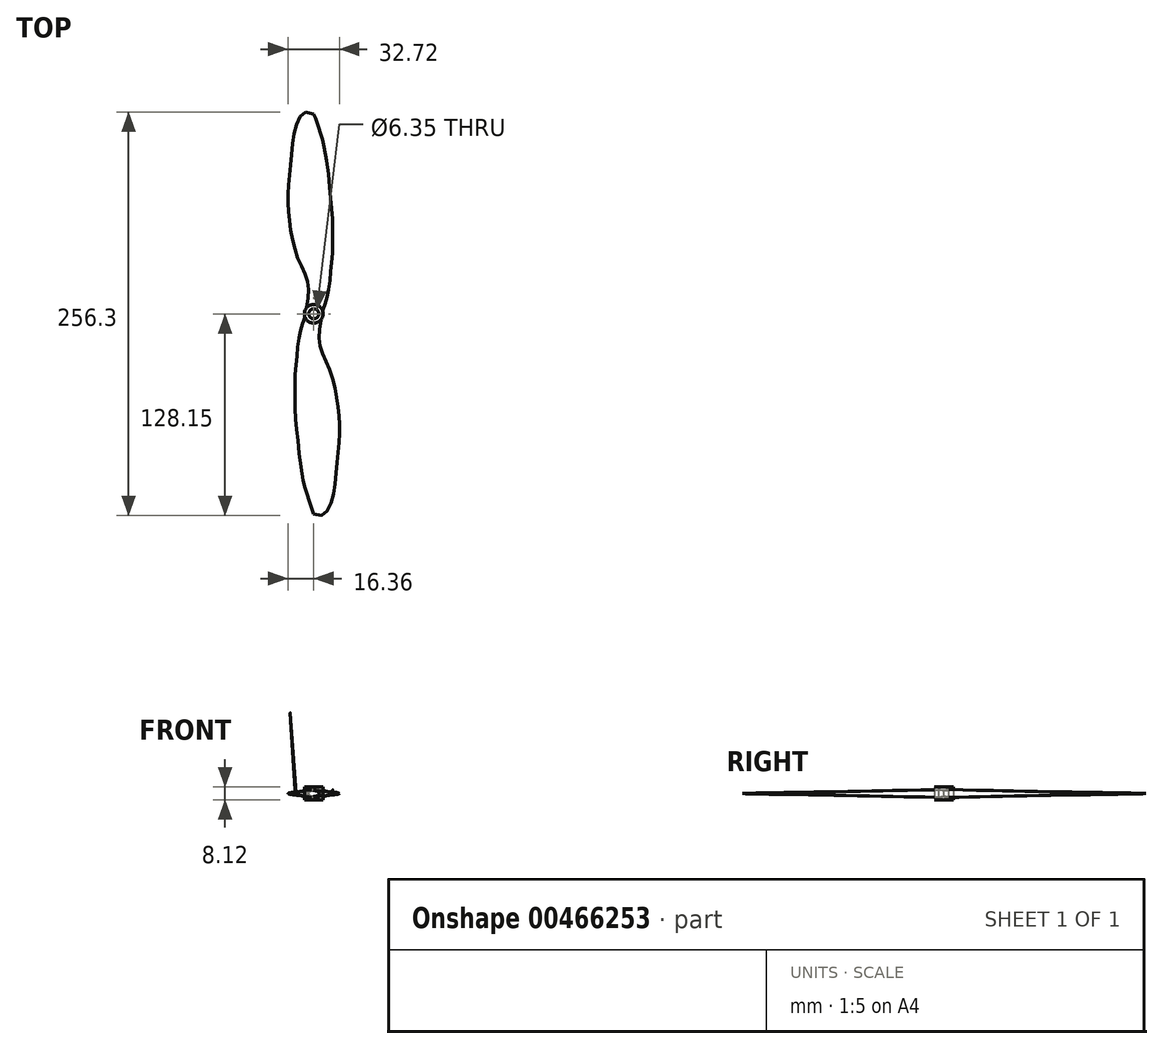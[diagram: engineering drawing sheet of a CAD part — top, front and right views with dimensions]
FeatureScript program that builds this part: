
annotation { "Feature Type Name" : "Feature", "Feature Type Description" : "" }
export const myFeature = defineFeature(function(context is Context, id is Id, definition is map)
    precondition{}
    {
        {
            var Q0;
            Q0=qCreatedBy(makeId("Front.planeOp"),FACE);
            var sketch = newSketch(context, id + "F0", { "sketchPlane" : qUnion([Q0])});
            skEllipse(sketch, "E0", {"center": v(0, 0) * mm, "majorRadius": 5.08 * mm, "minorRadius": 2.54 * mm, "majorAxis": v(-1, 0)});
            skSolve(sketch);
        }
        {
            var Q0;
            Q0=qCreatedBy(makeId("Front.planeOp"),FACE);
            cPlane(context, id + "F1", {"entities" : qUnion([Q0]), "cplaneType" : CPlaneType.OFFSET, "offset" : 127 * mm, "width" : 152.4 * mm, "height" : 152.4 * mm});
        }
        {
            var Q0;
            Q0=qCreatedBy(id+"F1.planeOp",FACE);
            var sketch = newSketch(context, id + "F2", { "sketchPlane" : qUnion([Q0])});
            skPoint(sketch, "E1", {"position": v(0, 0) * mm});
            skSolve(sketch);
        }
        {
            var Q0;
            Q0=qCreatedBy(makeId("Top.planeOp"),FACE);
            var sketch = newSketch(context, id + "F3", { "sketchPlane" : qUnion([Q0])});
            skFitSpline(sketch, "E2", {"points": [v(0, -127) * mm, v(9.95, -122.73) * mm, v(14.36, -99.28) * mm, v(16.33, -75.72) * mm, v(15.17, -57.1) * mm, v(10.15, -35.55) * mm, v(3.76, -19.58) * mm, v(5.08, 0) * mm], "startDerivative": vector(143.38, -80.7) * mm, "endDerivative": vector(20.49, 160.5) * mm});
            skFitSpline(sketch, "E3", {"points": [v(0, -127) * mm, v(-2.8, -119.45) * mm, v(-6.51, -106.64) * mm, v(-10.17, -79.93) * mm, v(-11.77, -61.82) * mm, v(-12.02, -50.3) * mm, v(-11.77, -37.54) * mm, v(-10.51, -24.52) * mm, v(-8.82, -12.2) * mm, v(-5.08, 0) * mm], "startDerivative": vector(-87.13, 232.18) * mm, "endDerivative": vector(23.36, 85.6) * mm});
            skSolve(sketch);
        }
        {
            var Q0;
            Q0=makeQuery(id+"F0.imprint","IMPRINT",FACE,{"disambiguationData":[TD([[makeQuery(id+"F0.imprint","IMPRINT",EDGE,{"derivedFrom":sQuery(id+"F0.wireOp",EDGE,"E0")}),1.0]])]});
            var Q1;
            Q1=sQuery(id+"F2.wireOp",VERTEX,"E1");
            var Q2;
            Q2=sQuery(id+"F3.wireOp",EDGE,"E3");
            var Q3;
            Q3=sQuery(id+"F3.wireOp",EDGE,"E2");
            loft(context, id + "F4", {"addGuides" : true, "sheetProfilesArray" : [{ "sheetProfileEntities" : qUnion([Q0]) }, { "sheetProfileEntities" : qUnion([Q1]) }], "guidesArray" : [{ "guideEntities" : qUnion([Q2]), "guideDerivativeType" : LoftGuideDerivativeType.DEFAULT, "guideDerivativeMagnitude" : 1 }, { "guideEntities" : qUnion([Q3]), "guideDerivativeType" : LoftGuideDerivativeType.DEFAULT, "guideDerivativeMagnitude" : 1 }]});
        }
        {
            var Q0;
            Q0=qCreatedBy(makeId("Top.planeOp"),FACE);
            var sketch = newSketch(context, id + "F5", { "sketchPlane" : qUnion([Q0])});
            skCircle(sketch, "E4", {"center": v(0, 0) * mm, "radius": 5.97 * mm});
            skCircle(sketch, "E5", {"center": v(0, 0) * mm, "radius": 3 * mm});
            skSolve(sketch);
        }
        {
            var Q0;
            Q0=qCreatedBy(makeId("Front.planeOp"),FACE);
            var sketch = newSketch(context, id + "F6", { "sketchPlane" : qUnion([Q0])});
            skLineSegment(sketch, "E6", {"start": v(0, 0) * mm, "end": v(0, 43.25) * mm});
            skSolve(sketch);
        }
        {
            var Q0;
            Q0=makeQuery(id+"F4.opLoft","SWEPT_BODY",BODY,{"disambiguationData":[OSD([makeQuery(id+"F0.imprint","IMPRINT",FACE,{"disambiguationData":[TD([[makeQuery(id+"F0.imprint","IMPRINT",EDGE,{"derivedFrom":sQuery(id+"F0.wireOp",EDGE,"E0")}),1.0]])]}),sQuery(id+"F2.wireOp",VERTEX,"E1"),sQuery(id+"F3.wireOp",EDGE,"E2"),sQuery(id+"F3.wireOp",EDGE,"E3")])]});
            var Q1;
            Q1=sQuery(id+"F6.wireOp",EDGE,"E6");
            circularPattern(context, id + "F7", {"entities" : qUnion([Q0]), "axis" : qUnion([Q1]), "angle" : 360 * degree, "instanceCount" : 2, "equalSpace" : true});
        }
        {
            var Q0;
            Q0=makeQuery(id+"F5.imprint","IMPRINT",FACE,{"disambiguationData":[TD([[makeQuery(id+"F5.imprint","IMPRINT",EDGE,{"derivedFrom":sQuery(id+"F5.wireOp",EDGE,"E4")}),1.0]])]});
            extrude(context, id + "F8", {"entities" : qUnion([Q0]), "endBound" : BoundingType.SYMMETRIC, "depth" : 8.13 * mm});
        }
        {
            var Q0;
            Q0=qCreatedBy(makeId("Top.planeOp"),FACE);
            cPlane(context, id + "F9", {"entities" : qUnion([Q0]), "cplaneType" : CPlaneType.OFFSET, "offset" : 25.4 * mm, "width" : 152.4 * mm, "height" : 152.4 * mm});
        }
        {
            var Q0;
            Q0=qCreatedBy(id+"F9.planeOp",FACE);
            var sketch = newSketch(context, id + "F10", { "sketchPlane" : qUnion([Q0])});
            skPoint(sketch, "E7", {"position": v(0, 0) * mm});
            skSolve(sketch);
        }
        {
            var Q0;
            Q0=sQuery(id+"F10.wireOp",VERTEX,"E7");
            var Q1;
            Q1=makeQuery(id+"F4.opLoft","SWEPT_BODY",BODY,{"disambiguationData":[OSD([makeQuery(id+"F0.imprint","IMPRINT",FACE,{"disambiguationData":[TD([[makeQuery(id+"F0.imprint","IMPRINT",EDGE,{"derivedFrom":sQuery(id+"F0.wireOp",EDGE,"E0")}),1.0]])]}),sQuery(id+"F2.wireOp",VERTEX,"E1"),sQuery(id+"F3.wireOp",EDGE,"E2"),sQuery(id+"F3.wireOp",EDGE,"E3")])]});
            var Q2;
            Q2=makeQuery(id+"F7.opPattern","COPY",BODY,{"derivedFrom":makeQuery(id+"F4.opLoft","SWEPT_BODY",BODY,{"disambiguationData":[OSD([makeQuery(id+"F0.imprint","IMPRINT",FACE,{"disambiguationData":[TD([[makeQuery(id+"F0.imprint","IMPRINT",EDGE,{"derivedFrom":sQuery(id+"F0.wireOp",EDGE,"E0")}),1.0]])]}),sQuery(id+"F2.wireOp",VERTEX,"E1"),sQuery(id+"F3.wireOp",EDGE,"E2"),sQuery(id+"F3.wireOp",EDGE,"E3")])]}),"instanceName":"1"});
            var Q3;
            Q3=makeQuery(id+"F8.opExtrude","SWEPT_BODY",BODY,{"disambiguationData":[OSD([sQuery(id+"F5.wireOp",EDGE,"E4"),sQuery(id+"F5.wireOp",EDGE,"E5")])]});
            hole(context, id + "F11", {"style" : HoleStyle.SIMPLE, "endStyle" : HoleEndStyle.THROUGH, "holeDiameter" : 6.35 * mm, "isTappedThrough" : true, "tappedDepth" : 12.7 * mm, "tapClearance" : 3, "locations" : qUnion([Q0]), "scope" : qUnion([Q1, Q2, Q3])});
        }
    });
